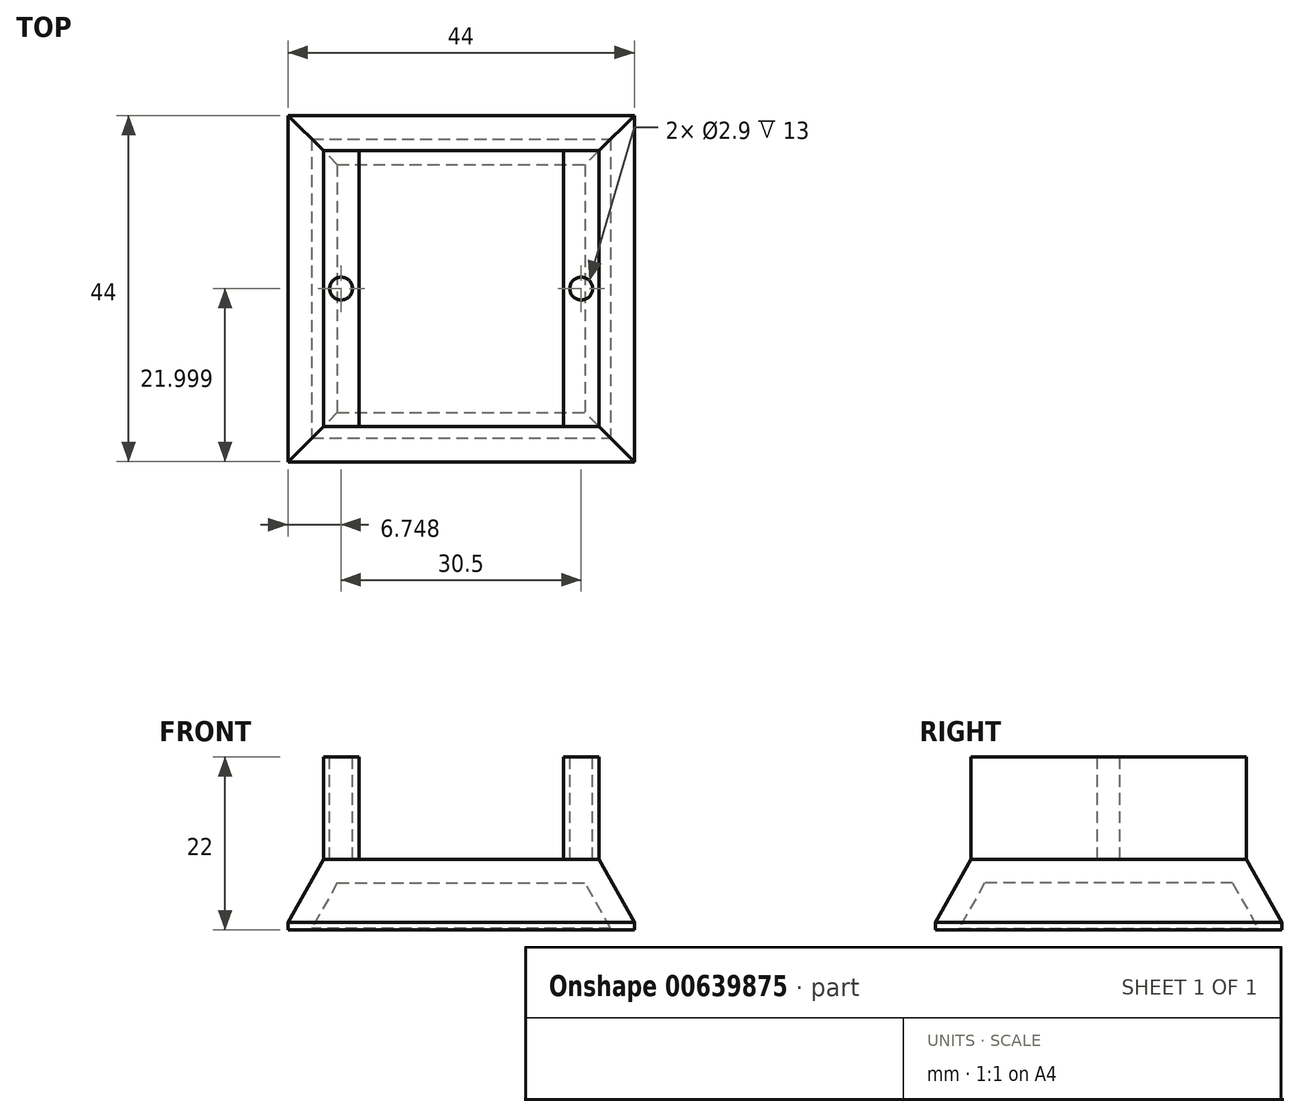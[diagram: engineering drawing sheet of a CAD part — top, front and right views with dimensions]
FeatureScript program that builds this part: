
annotation { "Feature Type Name" : "Feature", "Feature Type Description" : "" }
export const myFeature = defineFeature(function(context is Context, id is Id, definition is map)
    precondition{}
    {
        {
            var Q0;
            Q0=qCreatedBy(makeId("Top.planeOp"),FACE);
            var sketch = newSketch(context, id + "F0", { "sketchPlane" : qUnion([Q0])});
            skLineSegment(sketch, "E0.bottom", {"start": v(-18.85, 32.12) * mm, "end": v(25.15, 32.12) * mm});
            skLineSegment(sketch, "E0.top", {"start": v(-18.85, -11.88) * mm, "end": v(25.15, -11.88) * mm});
            skLineSegment(sketch, "E0.left", {"start": v(-18.85, 32.12) * mm, "end": v(-18.85, -11.88) * mm});
            skLineSegment(sketch, "E0.right", {"start": v(25.15, 32.12) * mm, "end": v(25.15, -11.88) * mm});
            skSolve(sketch);
        }
        {
            var Q0;
            Q0=makeQuery(id+"F0.imprint","IMPRINT",FACE,{"disambiguationData":[TD([[makeQuery(id+"F0.imprint","IMPRINT",EDGE,{"derivedFrom":sQuery(id+"F0.wireOp",EDGE,"E0.bottom")}),-1.0]])]});
            extrude(context, id + "F1", {"entities" : qUnion([Q0]), "depth" : 9 * mm, "offsetDistance" : 25 * mm});
        }
        {
            var Q0;
            Q0=makeQuery(id+"F1.opExtrude","CAP_EDGE",EDGE,{"disambiguationData":[OSD([sQuery(id+"F0.wireOp",EDGE,"E0.top")])],"isStart":false});
            var Q1;
            Q1=makeQuery(id+"F1.opExtrude","CAP_EDGE",EDGE,{"disambiguationData":[OSD([sQuery(id+"F0.wireOp",EDGE,"E0.left")])],"isStart":false});
            var Q2;
            Q2=makeQuery(id+"F1.opExtrude","CAP_EDGE",EDGE,{"disambiguationData":[OSD([sQuery(id+"F0.wireOp",EDGE,"E0.bottom")])],"isStart":false});
            var Q3;
            Q3=makeQuery(id+"F1.opExtrude","CAP_EDGE",EDGE,{"disambiguationData":[OSD([sQuery(id+"F0.wireOp",EDGE,"E0.right")])],"isStart":false});
            chamfer(context, id + "F2", {"entities" : qUnion([Q0, Q1, Q2, Q3]), "chamferType" : ChamferType.TWO_OFFSETS, "width1" : 4.5 * mm, "oppositeDirection" : false, "width2" : 8 * mm, "tangentPropagation" : true});
        }
        {
            var Q0;
            Q0=makeQuery(id+"F1.opExtrude","CAP_FACE",FACE,{"disambiguationData":[OSD([sQuery(id+"F0.wireOp",EDGE,"E0.bottom"),sQuery(id+"F0.wireOp",EDGE,"E0.top"),sQuery(id+"F0.wireOp",EDGE,"E0.left"),sQuery(id+"F0.wireOp",EDGE,"E0.right")])],"isStart":false});
            var sketch = newSketch(context, id + "F3", { "sketchPlane" : qUnion([Q0])});
            skLineSegment(sketch, "E1.1", {"start": v(20.65, 27.62) * mm, "end": v(-14.35, 27.62) * mm, "construction": true});
            skLineSegment(sketch, "E1.2", {"start": v(-14.35, -7.38) * mm, "end": v(20.65, -7.38) * mm, "construction": true});
            skLineSegment(sketch, "E1.3", {"start": v(-14.35, 27.62) * mm, "end": v(-14.35, -7.38) * mm, "construction": true});
            skLineSegment(sketch, "E1.4", {"start": v(20.65, -7.38) * mm, "end": v(20.65, 27.62) * mm, "construction": true});
            skLineSegment(sketch, "E2", {"start": v(-14.35, 10.12) * mm, "end": v(20.65, 10.12) * mm, "construction": true});
            skLineSegment(sketch, "E3", {"start": v(3.15, 27.62) * mm, "end": v(3.15, -7.38) * mm, "construction": true});
            skLineSegment(sketch, "E4.bottom", {"start": v(-14.35, 27.62) * mm, "end": v(20.65, 27.62) * mm});
            skLineSegment(sketch, "E4.top", {"start": v(-14.35, -7.38) * mm, "end": v(20.65, -7.38) * mm});
            skLineSegment(sketch, "E4.left", {"start": v(-14.35, 27.62) * mm, "end": v(-14.35, -7.38) * mm});
            skLineSegment(sketch, "E4.right", {"start": v(20.65, 27.62) * mm, "end": v(20.65, -7.38) * mm});
            skPoint(sketch, "E4.middle", {"position": v(3.15, 10.12) * mm});
            skSolve(sketch);
        }
        {
            var Q0;
            Q0=makeQuery(id+"F1.opExtrude","CAP_FACE",FACE,{"disambiguationData":[OSD([sQuery(id+"F0.wireOp",EDGE,"E0.bottom"),sQuery(id+"F0.wireOp",EDGE,"E0.top"),sQuery(id+"F0.wireOp",EDGE,"E0.left"),sQuery(id+"F0.wireOp",EDGE,"E0.right")])],"isStart":true});
            shell(context, id + "F4", {"entities" : qUnion([Q0]), "thickness" : 3 * mm});
        }
        {
            var Q0;
            Q0=makeQuery(id+"F3.imprint","IMPRINT",FACE,{"disambiguationData":[TD([[makeQuery(id+"F3.imprint","IMPRINT",EDGE,{"derivedFrom":sQuery(id+"F3.wireOp",EDGE,"E4.bottom")}),1.0]])]});
            var sketch = newSketch(context, id + "F5", { "sketchPlane" : qUnion([Q0])});
            skLineSegment(sketch, "E5.0", {"start": v(3.15, 27.62) * mm, "end": v(3.15, -7.38) * mm, "construction": true});
            skLineSegment(sketch, "E5.1", {"start": v(-14.35, 10.12) * mm, "end": v(20.65, 10.12) * mm, "construction": true});
            skLineSegment(sketch, "E6.left", {"start": v(16.15, -7.38) * mm, "end": v(16.15, 27.62) * mm});
            skLineSegment(sketch, "E6.right", {"start": v(-9.85, -7.38) * mm, "end": v(-9.85, 27.62) * mm});
            skPoint(sketch, "E6.middle", {"position": v(3.15, 10.12) * mm});
            skLineSegment(sketch, "E7.0", {"start": v(-14.35, 27.62) * mm, "end": v(-9.85, 27.62) * mm});
            skLineSegment(sketch, "E7.1", {"start": v(-14.35, 27.62) * mm, "end": v(-14.35, -7.38) * mm});
            skLineSegment(sketch, "E7.2", {"start": v(20.65, 27.62) * mm, "end": v(20.65, -7.38) * mm});
            skLineSegment(sketch, "E7.3", {"start": v(-14.35, -7.38) * mm, "end": v(-9.85, -7.38) * mm});
            skLineSegment(sketch, "E8.trimOffspring", {"start": v(16.15, 27.62) * mm, "end": v(20.65, 27.62) * mm});
            skLineSegment(sketch, "E9.trimOffspring", {"start": v(16.15, -7.38) * mm, "end": v(20.65, -7.38) * mm});
            skSolve(sketch);
        }
        {
            var Q0;
            Q0 = qSketchRegion(id + "F5", true);
            extrude(context, id + "F6", {"entities" : qUnion([Q0]), "operationType" : NewBodyOperationType.ADD, "depth" : 13 * mm, "offsetDistance" : 25 * mm});
        }
        {
            var Q0;
            Q0=makeQuery(id+"F6.opExtrude","CAP_FACE",FACE,{"disambiguationData":[OSD([sQuery(id+"F5.wireOp",EDGE,"E6.right"),sQuery(id+"F5.wireOp",EDGE,"E7.0"),sQuery(id+"F5.wireOp",EDGE,"E7.1"),sQuery(id+"F5.wireOp",EDGE,"E7.3")])],"isStart":false});
            var sketch = newSketch(context, id + "F7", { "sketchPlane" : qUnion([Q0])});
            skLineSegment(sketch, "E10.0", {"start": v(-14.35, 10.12) * mm, "end": v(20.65, 10.12) * mm, "construction": true});
            skLineSegment(sketch, "E10.1", {"start": v(-14.35, 27.62) * mm, "end": v(-9.85, 27.62) * mm});
            skLineSegment(sketch, "E10.2", {"start": v(16.15, 27.62) * mm, "end": v(20.65, 27.62) * mm});
            skLineSegment(sketch, "E11", {"start": v(-12.1, 27.62) * mm, "end": v(-12.1, -7.38) * mm, "construction": true});
            skLineSegment(sketch, "E12", {"start": v(18.4, 27.62) * mm, "end": v(18.4, -7.5) * mm, "construction": true});
            skCircle(sketch, "E13", {"center": v(-12.1, 10.12) * mm, "radius": 1.45 * mm});
            skCircle(sketch, "E14", {"center": v(18.4, 10.12) * mm, "radius": 1.45 * mm});
            skSolve(sketch);
        }
        {
            var Q0;
            Q0=makeQuery(id+"F7.imprint","IMPRINT",FACE,{"disambiguationData":[TD([[makeQuery(id+"F7.imprint","IMPRINT",EDGE,{"derivedFrom":sQuery(id+"F7.wireOp",EDGE,"E13")}),1.0]])]});
            var Q1;
            Q1=makeQuery(id+"F7.imprint","IMPRINT",FACE,{"disambiguationData":[TD([[makeQuery(id+"F7.imprint","IMPRINT",EDGE,{"derivedFrom":sQuery(id+"F7.wireOp",EDGE,"E14")}),1.0]])]});
            extrude(context, id + "F8", {"entities" : qUnion([Q0, Q1]), "operationType" : NewBodyOperationType.REMOVE, "oppositeDirection" : true, "depth" : 13 * mm, "offsetDistance" : 25 * mm});
        }
    });
